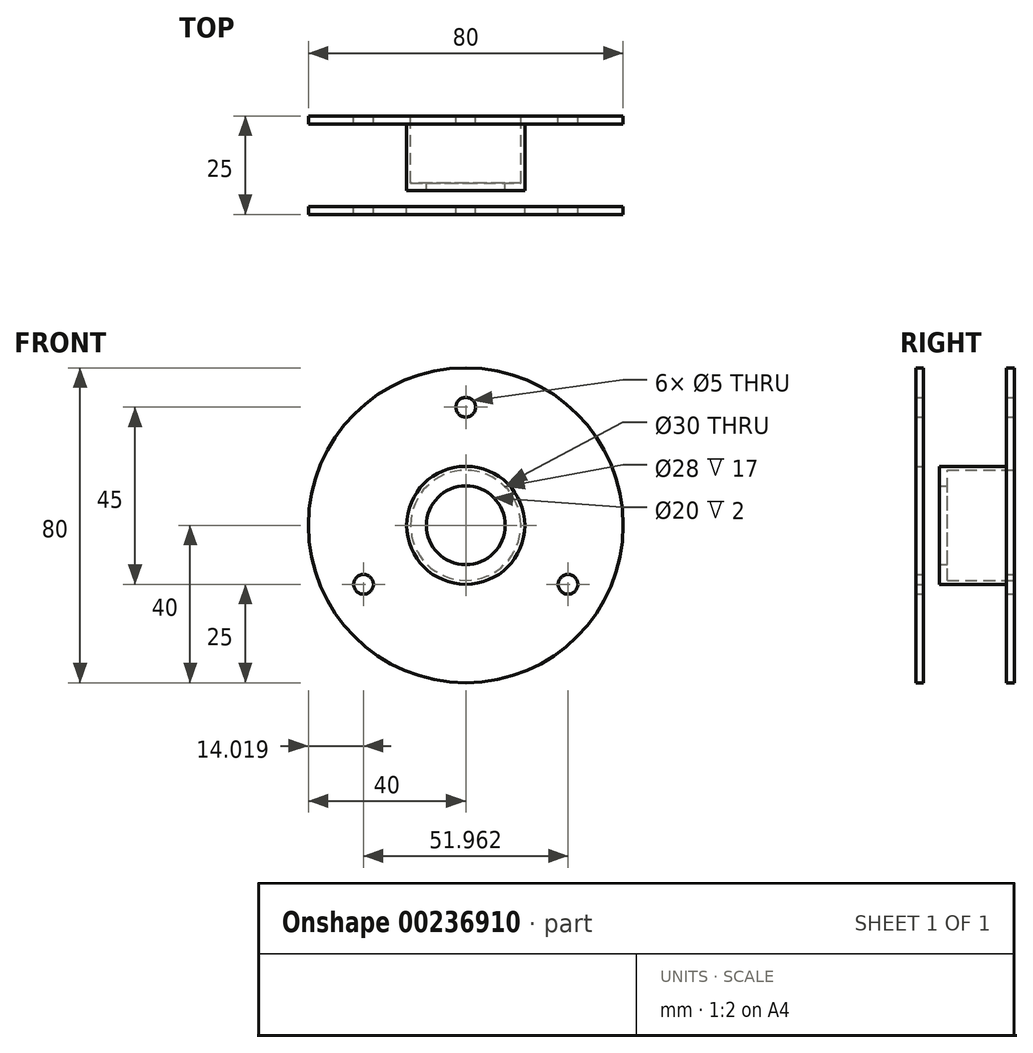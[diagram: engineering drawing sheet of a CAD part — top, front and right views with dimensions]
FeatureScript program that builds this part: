
annotation { "Feature Type Name" : "Feature", "Feature Type Description" : "" }
export const myFeature = defineFeature(function(context is Context, id is Id, definition is map)
    precondition{}
    {
        {
            var Q0;
            Q0=qCreatedBy(makeId("Front.planeOp"),FACE);
            var sketch = newSketch(context, id + "F0", { "sketchPlane" : qUnion([Q0])});
            skLineSegment(sketch, "E0", {"start": v(-119.26, 0) * mm, "end": v(-130, 0) * mm, "construction": true});
            skCircle(sketch, "E1", {"center": v(-130, 0) * mm, "radius": 10 * mm});
            skCircle(sketch, "E2", {"center": v(-130, 0) * mm, "radius": 14 * mm});
            skCircle(sketch, "E3", {"center": v(-130, 0) * mm, "radius": 15 * mm});
            skCircle(sketch, "E4", {"center": v(-130, 0) * mm, "radius": 40 * mm});
            skLineSegment(sketch, "E5", {"start": v(0, 0) * mm, "end": v(-130, 0) * mm, "construction": true});
            skLineSegment(sketch, "E6", {"start": v(-130, 0) * mm, "end": v(-130, 30) * mm, "construction": true});
            skCircle(sketch, "E7", {"center": v(-130, 30) * mm, "radius": 2.5 * mm});
            skCircle(sketch, "E8.1.0", {"center": v(-155.98, -15) * mm, "radius": 2.5 * mm});
            skLineSegment(sketch, "E8.1.1", {"start": v(-130, 0) * mm, "end": v(-155.98, -15) * mm, "construction": true});
            skCircle(sketch, "E8.2.0", {"center": v(-104.02, -15) * mm, "radius": 2.5 * mm});
            skLineSegment(sketch, "E8.2.1", {"start": v(-130, 0) * mm, "end": v(-104.02, -15) * mm, "construction": true});
            skSolve(sketch);
        }
        {
            var Q0;
            Q0=makeQuery(id+"F0.imprint","IMPRINT",FACE,{"disambiguationData":[TD([[makeQuery(id+"F0.imprint","IMPRINT",EDGE,{"derivedFrom":sQuery(id+"F0.wireOp",EDGE,"E3")}),-1.0]])]});
            extrude(context, id + "F1", {"entities" : qUnion([Q0]), "depth" : 2 * mm});
        }
        {
            var Q0;
            Q0=makeQuery(id+"F0.imprint","IMPRINT",FACE,{"disambiguationData":[TD([[makeQuery(id+"F0.imprint","IMPRINT",EDGE,{"derivedFrom":sQuery(id+"F0.wireOp",EDGE,"E2")}),-1.0]])]});
            extrude(context, id + "F2", {"entities" : qUnion([Q0]), "operationType" : NewBodyOperationType.ADD, "depth" : 19 * mm});
        }
        {
            var Q0;
            Q0=makeQuery(id+"F0.imprint","IMPRINT",FACE,{"disambiguationData":[TD([[makeQuery(id+"F0.imprint","IMPRINT",EDGE,{"derivedFrom":sQuery(id+"F0.wireOp",EDGE,"E1")}),-1.0]])]});
            extrude(context, id + "F3", {"entities" : qUnion([Q0]), "operationType" : NewBodyOperationType.ADD, "depth" : 19 * mm, "hasSecondDirection" : true, "secondDirectionOppositeDirection" : false, "secondDirectionDepth" : 17 * mm});
        }
        {
            var Q0;
            Q0=makeQuery(id+"F0.imprint","IMPRINT",FACE,{"disambiguationData":[TD([[makeQuery(id+"F0.imprint","IMPRINT",EDGE,{"derivedFrom":sQuery(id+"F0.wireOp",EDGE,"E3")}),-1.0]])]});
            extrude(context, id + "F4", {"entities" : qUnion([Q0]), "depth" : 25 * mm, "hasSecondDirection" : true, "secondDirectionOppositeDirection" : false, "secondDirectionDepth" : 23 * mm});
        }
    });
